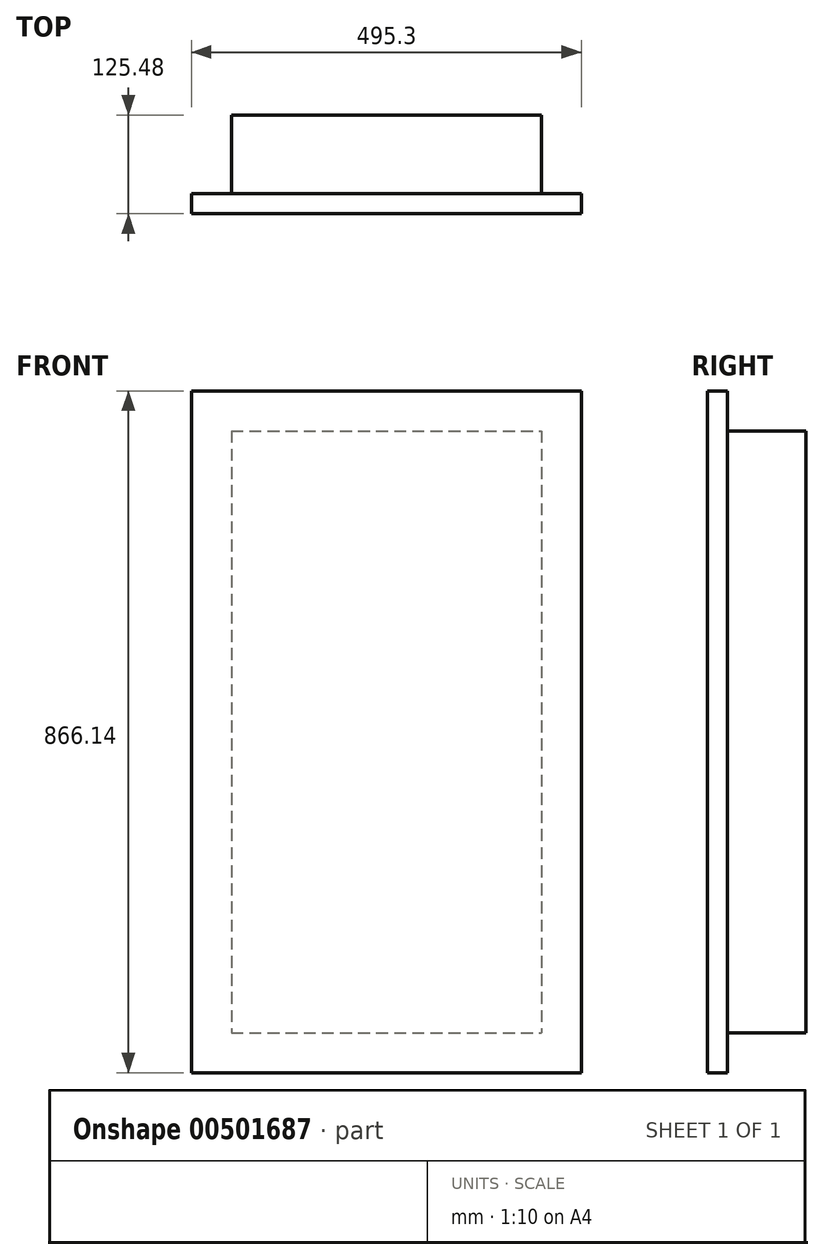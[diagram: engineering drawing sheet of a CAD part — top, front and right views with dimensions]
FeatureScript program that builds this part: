
annotation { "Feature Type Name" : "Feature", "Feature Type Description" : "" }
export const myFeature = defineFeature(function(context is Context, id is Id, definition is map)
    precondition{}
    {
        {
            var Q0;
            Q0=qCreatedBy(makeId("Front.planeOp"),FACE);
            var sketch = newSketch(context, id + "F0", { "sketchPlane" : qUnion([Q0])});
            skLineSegment(sketch, "E0.bottom", {"start": v(247.65, 433.07) * mm, "end": v(-247.65, 433.07) * mm});
            skLineSegment(sketch, "E0.top", {"start": v(247.65, -433.07) * mm, "end": v(-247.65, -433.07) * mm});
            skLineSegment(sketch, "E0.left", {"start": v(247.65, 433.07) * mm, "end": v(247.65, -433.07) * mm});
            skLineSegment(sketch, "E0.right", {"start": v(-247.65, 433.07) * mm, "end": v(-247.65, -433.07) * mm});
            skPoint(sketch, "E0.middle", {"position": v(0, 0) * mm});
            skSolve(sketch);
        }
        {
            var Q0;
            Q0 = qSketchRegion(id + "F0", true);
            extrude(context, id + "F1", {"entities" : qUnion([Q0]), "depth" : 25.4 * mm});
        }
        {
            var Q0;
            Q0=makeQuery(id+"F1.opExtrude","CAP_FACE",FACE,{"disambiguationData":[OSD([sQuery(id+"F0.wireOp",EDGE,"E0.bottom"),sQuery(id+"F0.wireOp",EDGE,"E0.top"),sQuery(id+"F0.wireOp",EDGE,"E0.left"),sQuery(id+"F0.wireOp",EDGE,"E0.right")])],"isStart":true});
            var sketch = newSketch(context, id + "F2", { "sketchPlane" : qUnion([Q0])});
            skLineSegment(sketch, "E1.bottom", {"start": v(196.85, 382.27) * mm, "end": v(-196.85, 382.27) * mm});
            skLineSegment(sketch, "E1.top", {"start": v(196.85, -382.27) * mm, "end": v(-196.85, -382.27) * mm});
            skLineSegment(sketch, "E1.left", {"start": v(196.85, 382.27) * mm, "end": v(196.85, -382.27) * mm});
            skLineSegment(sketch, "E1.right", {"start": v(-196.85, 382.27) * mm, "end": v(-196.85, -382.27) * mm});
            skPoint(sketch, "E1.middle", {"position": v(0, 0) * mm});
            skSolve(sketch);
        }
        {
            var Q0;
            Q0 = qSketchRegion(id + "F2", true);
            extrude(context, id + "F3", {"entities" : qUnion([Q0]), "operationType" : NewBodyOperationType.ADD, "depth" : 100.08 * mm});
        }
    });
